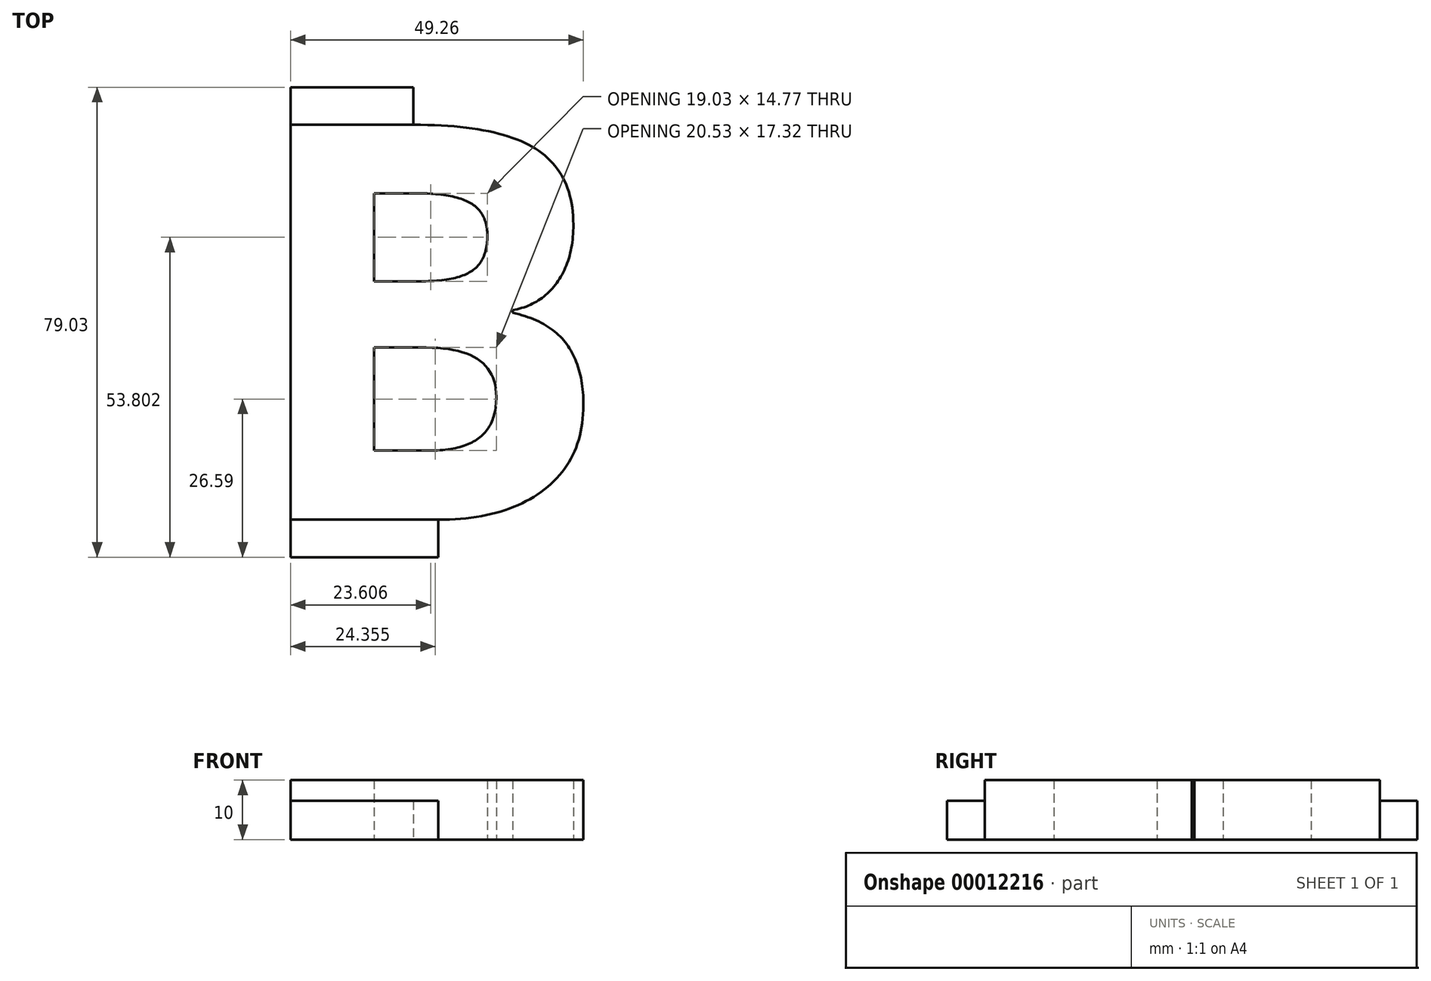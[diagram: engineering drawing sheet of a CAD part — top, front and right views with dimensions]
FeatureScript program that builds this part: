
annotation { "Feature Type Name" : "Feature", "Feature Type Description" : "" }
export const myFeature = defineFeature(function(context is Context, id is Id, definition is map)
    precondition{}
    {
        {
            var Q0;
            Q0=qCreatedBy(makeId("Top.planeOp"),FACE);
            var sketch = newSketch(context, id + "F0", { "sketchPlane" : qUnion([Q0])});
            skText(sketch, "E0", { "text": "B", "fontName": "OpenSans-Bold.ttf"});
            const initialGuessF0  = {"E0": [-0.05762, 0, 1, 0, 0.067]};
            skSetInitialGuess(sketch, initialGuessF0);
            skSolve(sketch);
        }
        {
            var Q0;
            Q0=makeQuery(id+"F0.imprint","IMPRINT",FACE,{"disambiguationData":[TD([[makeQuery(id+"F0.imprint","IMPRINT",EDGE,{"derivedFrom":sQuery(id+"F0.wireOp",EDGE,"E0.sketch_text.stroke-0")}),-1.0]])]});
            extrude(context, id + "F1", {"entities" : qUnion([Q0]), "depth" : 10 * mm});
        }
        {
            var Q0;
            Q0=makeQuery(id+"F1.opExtrude","SWEPT_FACE",FACE,{"disambiguationData":[OSD([sQuery(id+"F0.wireOp",EDGE,"E0.sketch_text.stroke-10")])]});
            var sketch = newSketch(context, id + "F2", { "sketchPlane" : qUnion([Q0])});
            skLineSegment(sketch, "E1.0.0", {"start": v(-49.26, 0) * mm, "end": v(-24.41, 0) * mm});
            skLineSegment(sketch, "E1.0.1", {"start": v(-24.41, 0) * mm, "end": v(-24.41, 10) * mm});
            skLineSegment(sketch, "E1.0.2", {"start": v(-24.41, 10) * mm, "end": v(-49.26, 10) * mm});
            skLineSegment(sketch, "E1.0.3", {"start": v(-49.26, 10) * mm, "end": v(-49.26, 0) * mm});
            skLineSegment(sketch, "E2.top", {"start": v(-49.26, 6.5) * mm, "end": v(-24.41, 6.5) * mm});
            skLineSegment(sketch, "E2.left", {"start": v(-49.26, 0) * mm, "end": v(-49.26, 6.5) * mm});
            skLineSegment(sketch, "E2.right", {"start": v(-24.41, 0) * mm, "end": v(-24.41, 6.5) * mm});
            skSolve(sketch);
        }
        {
            var Q0;
            Q0=makeQuery(id+"F2.imprint","IMPRINT",FACE,{"disambiguationData":[TD([[makeQuery(id+"F2.imprint","IMPRINT",EDGE,{"derivedFrom":sQuery(id+"F2.wireOp",EDGE,"E1.0.0")}),-1.0]])]});
            extrude(context, id + "F3", {"entities" : qUnion([Q0]), "operationType" : NewBodyOperationType.ADD, "depth" : 6.3 * mm});
        }
        {
            var Q0;
            Q0=makeQuery(id+"F1.opExtrude","SWEPT_FACE",FACE,{"disambiguationData":[OSD([sQuery(id+"F0.wireOp",EDGE,"E0.sketch_text.stroke-0")])]});
            var sketch = newSketch(context, id + "F4", { "sketchPlane" : qUnion([Q0])});
            skLineSegment(sketch, "E3.0.0", {"start": v(28.59, 0) * mm, "end": v(49.26, 0) * mm});
            skLineSegment(sketch, "E3.0.1", {"start": v(49.26, 0) * mm, "end": v(49.26, 10) * mm});
            skLineSegment(sketch, "E3.0.2", {"start": v(49.26, 10) * mm, "end": v(28.59, 10) * mm});
            skLineSegment(sketch, "E3.0.3", {"start": v(28.59, 10) * mm, "end": v(28.59, 0) * mm});
            skLineSegment(sketch, "E4.top", {"start": v(28.59, 6.5) * mm, "end": v(49.26, 6.5) * mm});
            skLineSegment(sketch, "E4.left", {"start": v(28.59, 0) * mm, "end": v(28.59, 6.5) * mm});
            skLineSegment(sketch, "E4.right", {"start": v(49.26, 0) * mm, "end": v(49.26, 6.5) * mm});
            skSolve(sketch);
        }
        {
            var Q0;
            Q0=makeQuery(id+"F4.imprint","IMPRINT",FACE,{"disambiguationData":[TD([[makeQuery(id+"F4.imprint","IMPRINT",EDGE,{"derivedFrom":sQuery(id+"F4.wireOp",EDGE,"E3.0.0")}),-1.0]])]});
            extrude(context, id + "F5", {"entities" : qUnion([Q0]), "operationType" : NewBodyOperationType.ADD, "depth" : 6.3 * mm});
        }
    });
